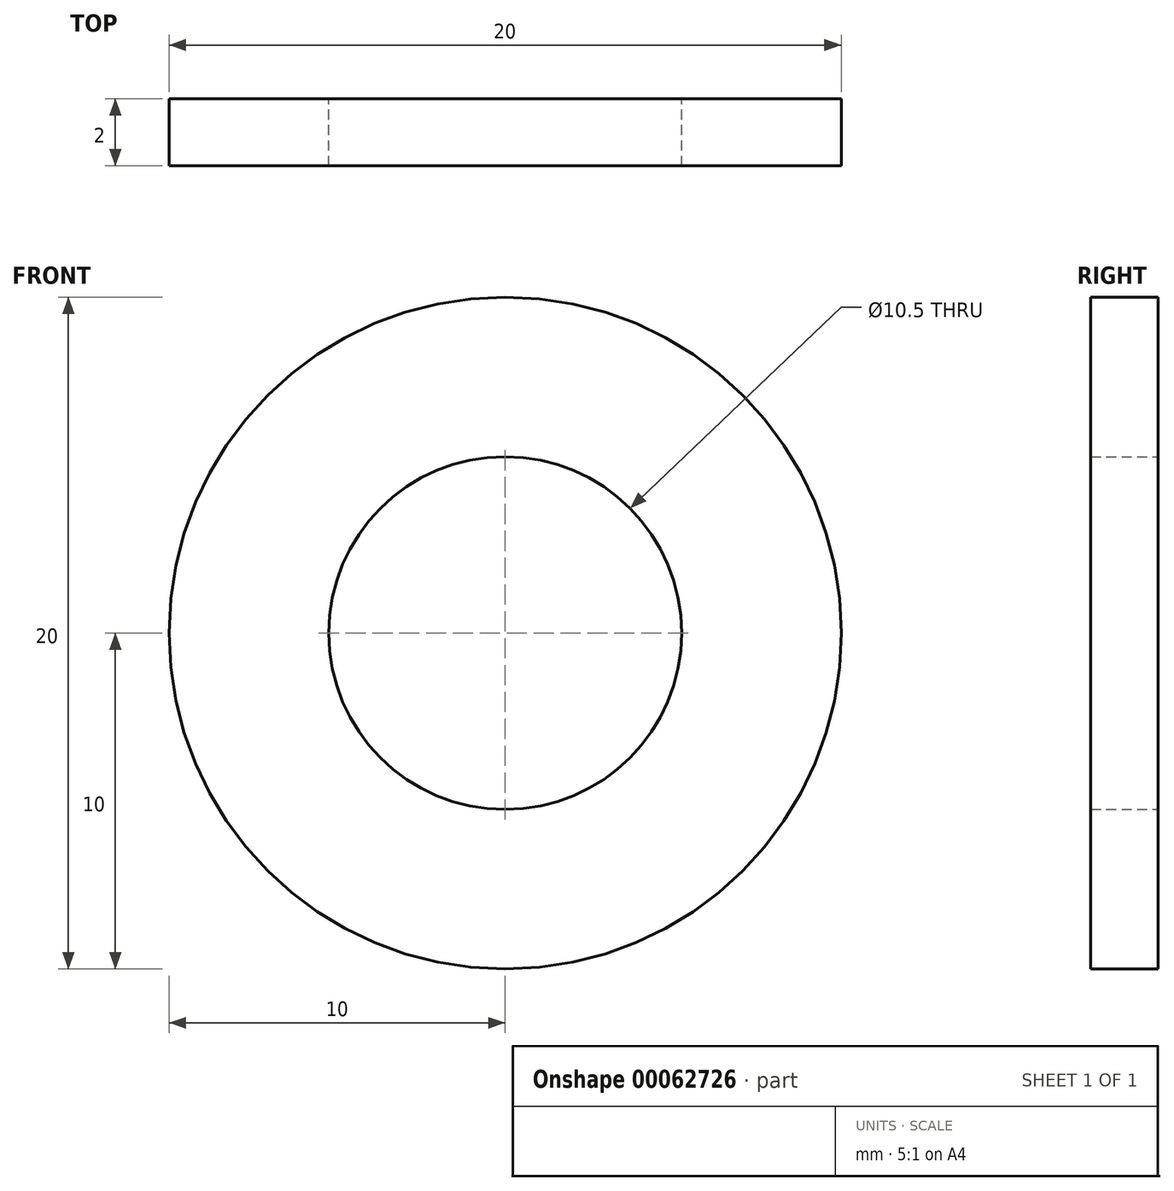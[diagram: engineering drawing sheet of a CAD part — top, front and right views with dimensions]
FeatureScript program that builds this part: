
annotation { "Feature Type Name" : "Feature", "Feature Type Description" : "" }
export const myFeature = defineFeature(function(context is Context, id is Id, definition is map)
    precondition{}
    {
        {
            var Q0;
            Q0=qCreatedBy(makeId("Front.planeOp"),FACE);
            var sketch = newSketch(context, id + "F0", { "sketchPlane" : qUnion([Q0])});
            skCircle(sketch, "E0", {"center": v(0, 0) * mm, "radius": 10 * mm});
            skCircle(sketch, "E1", {"center": v(0, 0) * mm, "radius": 5.25 * mm});
            skSolve(sketch);
        }
        {
            var Q0;
            Q0=makeQuery(id+"F0.imprint","IMPRINT",FACE,{"disambiguationData":[TD([[makeQuery(id+"F0.imprint","IMPRINT",EDGE,{"derivedFrom":sQuery(id+"F0.wireOp",EDGE,"E0")}),1.0]])]});
            extrude(context, id + "F1", {"entities" : qUnion([Q0]), "depth" : 2 * mm});
        }
    });
